# Revit family: Network IO Expander-Audio-Q-SYS-QIO-TEL2
name_source: partatom
category: Communication Devices
units: mm (PartAtom-declared; Revit-internal decimal feet)

## family parameters
Cut with Voids When Loaded = No
Host = Face
Maintain Annotation Orientation = No
OmniClass Number = 23.85.10.17.11
OmniClass Title = Audio-Visual System Components
Part Type = Normal
Room Calculation Point = No
Round Connector Dimension = Use Diameter
Shared = No

## types (1)
- TEL2
    Apparent Load = 67 VA
    Body Material = Paint - Q-SYS - Black
    Body Offset = 0 mm  [stored 0 ft]
    Body Width = 109 mm  [stored 0.357612 ft]
    Default Elevation = 1219.2 mm
    Depth = 215.9 mm  [stored 0.708333 ft]
    Description = Surface mounted analog telephony expander for Q-SYS platform.
    Frame Depth = 2 mm  [stored 0.00656168 ft]
    Grille Material = Paint - Q-SYS - Black Mesh 2
    Height = 42.4 mm  [stored 0.139108 ft]
    Highlight Material = Plastic - Q-SYS - Black
    IQ Category = Network IO Expander
    LED Material = Plastic - Q-SYS - LED Blue
    Length 1 = 3 mm  [stored 0.00984252 ft]
    Load Classification = Other
    Manufacturer = Q-SYS
    Manufacturer URL = https://www.qsys.com
    Minimum Circuit Amps = 3 A
    Model = TEL2
    Number of Poles = 2
    Power Factor = 0.9
    Product Documentation Link = https://www.qsys.com
    Product Page URL = https://www.qsys.com
    Type Comments = TEL2
    URL = https://www.qsys.com
    Voltage = 24 V
    Weight = 1.63 lbm
    Weight Dimensional = 1.63
    Weight Product = 1.63
    Width = 109 mm  [stored 0.357612 ft]

note: [stored X ft] marks values corroborated as IEEE doubles in the binary element streams (Revit-internal decimal feet)

## geometry (parser evidence)
native form markers: Sweep x2
no freeform markers — native parametric forms only
